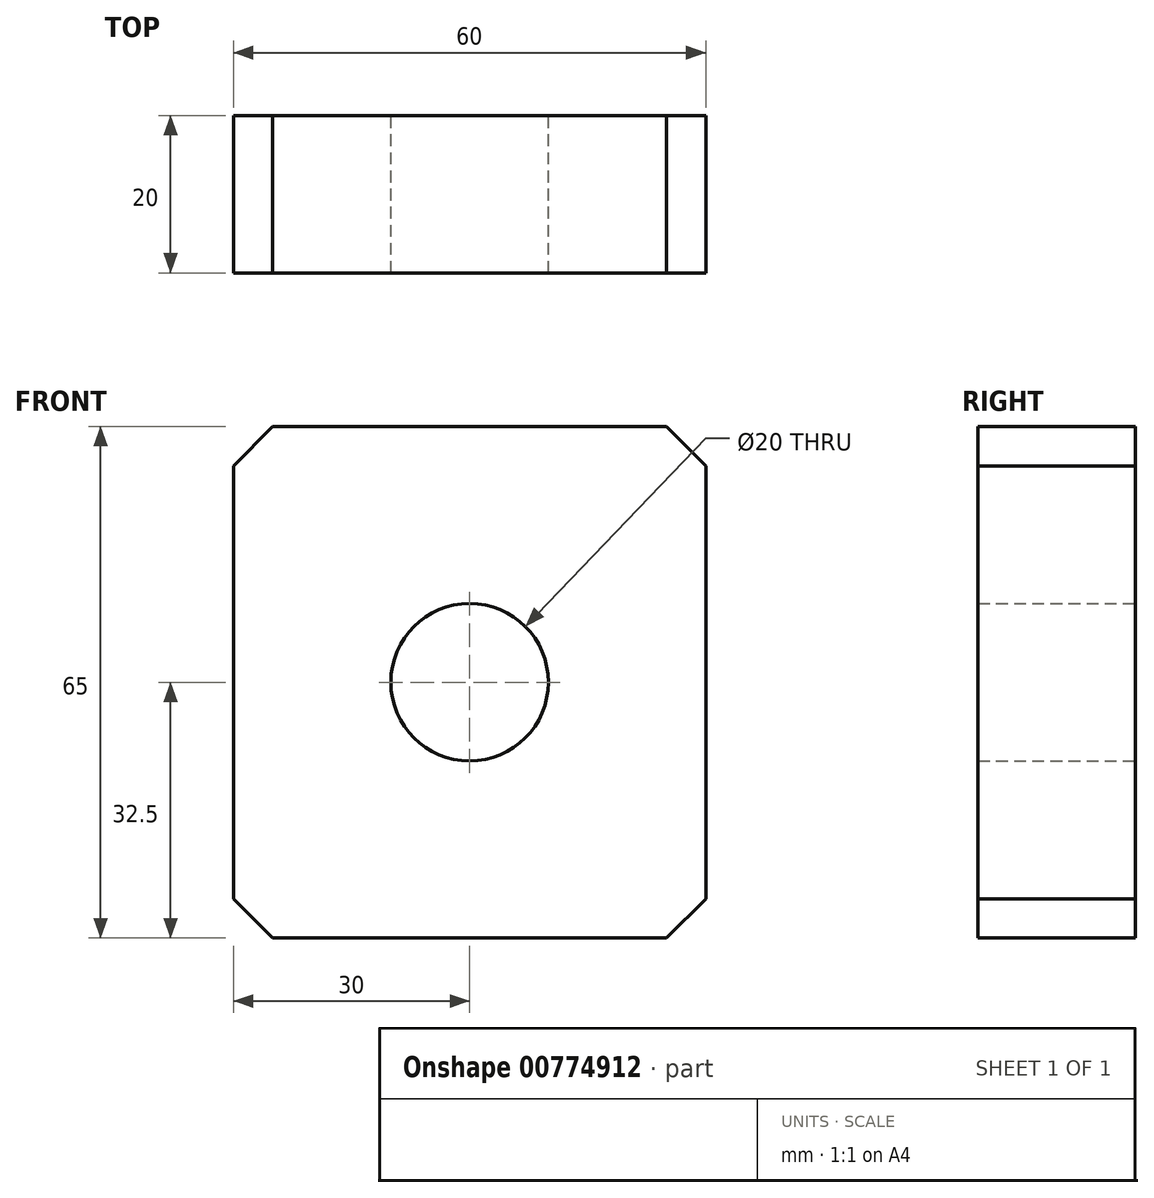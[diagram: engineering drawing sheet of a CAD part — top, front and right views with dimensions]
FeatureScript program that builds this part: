
annotation { "Feature Type Name" : "Feature", "Feature Type Description" : "" }
export const myFeature = defineFeature(function(context is Context, id is Id, definition is map)
    precondition{}
    {
        {
            var Q0;
            Q0=qCreatedBy(makeId("Front.planeOp"),FACE);
            var sketch = newSketch(context, id + "F0", { "sketchPlane" : qUnion([Q0])});
            skLineSegment(sketch, "E0.bottom", {"start": v(-30, 32.5) * mm, "end": v(30, 32.5) * mm});
            skLineSegment(sketch, "E0.top", {"start": v(-30, -32.5) * mm, "end": v(30, -32.5) * mm});
            skLineSegment(sketch, "E0.left", {"start": v(-30, 32.5) * mm, "end": v(-30, -32.5) * mm});
            skLineSegment(sketch, "E0.right", {"start": v(30, 32.5) * mm, "end": v(30, -32.5) * mm});
            skPoint(sketch, "E0.middle", {"position": v(0, 0) * mm});
            skCircle(sketch, "E1", {"center": v(0, 0) * mm, "radius": 10 * mm});
            skSolve(sketch);
        }
        {
            var Q0;
            Q0=makeQuery(id+"F0.imprint","IMPRINT",FACE,{"disambiguationData":[TD([[makeQuery(id+"F0.imprint","IMPRINT",EDGE,{"derivedFrom":sQuery(id+"F0.wireOp",EDGE,"E0.bottom")}),-1.0]])]});
            extrude(context, id + "F1", {"entities" : qUnion([Q0]), "depth" : 20 * mm, "offsetDistance" : 25 * mm});
        }
        {
            var Q0;
            Q0=makeQuery(id+"F1.opExtrude","SWEPT_EDGE",EDGE,{"disambiguationData":[OSD([sQuery(id+"F0.wireOp",EDGE,"E0.top"),sQuery(id+"F0.wireOp",EDGE,"E0.left")])]});
            var Q1;
            Q1=makeQuery(id+"F1.opExtrude","SWEPT_EDGE",EDGE,{"disambiguationData":[OSD([sQuery(id+"F0.wireOp",EDGE,"E0.bottom"),sQuery(id+"F0.wireOp",EDGE,"E0.left")])]});
            var Q2;
            Q2=makeQuery(id+"F1.opExtrude","SWEPT_EDGE",EDGE,{"disambiguationData":[OSD([sQuery(id+"F0.wireOp",EDGE,"E0.top"),sQuery(id+"F0.wireOp",EDGE,"E0.right")])]});
            var Q3;
            Q3=makeQuery(id+"F1.opExtrude","SWEPT_EDGE",EDGE,{"disambiguationData":[OSD([sQuery(id+"F0.wireOp",EDGE,"E0.bottom"),sQuery(id+"F0.wireOp",EDGE,"E0.right")])]});
            chamfer(context, id + "F2", {"entities" : qUnion([Q0, Q1, Q2, Q3]), "width" : 5 * mm, "tangentPropagation" : true});
        }
    });
